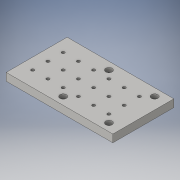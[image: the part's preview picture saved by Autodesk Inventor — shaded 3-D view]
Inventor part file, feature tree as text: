
AUTODESK INVENTOR PART (.ipt)
format: ipt  version: 2016 (Build 200138000, 138)  size: 142,336 bytes
history: native  units: mm
features: sketch x3, hole x2, projected_geometry x2, extrude x1
ambient origin geometry x8: Origin, YZ Plane, XZ Plane, XY Plane, X Axis, Y Axis, Z Axis, Center Point
bodies: Solid1 (feature_tree)
feature tree (8):
  extrude  "Extrusion1"  Depth=100.0mm
  hole  "Hole1"  [1 undecoded]
  hole  "Hole2"  [1 undecoded]
  sketch  "Sketch1"  dims[d0=100.0mm d1=56.5mm]
  sketch  "Sketch2"  dims[d2=175.0mm d3=12.5mm d4=0.0mm]
  projected_geometry  "Projected Loop1"
  sketch  "Sketch3"  dims[d5=75.0mm d6=75.0mm d7=6.0mm d8=6.0mm d9=10.5mm d10=7.0mm d11=90.0deg d12=8.0mm d13=20.594885mm d14=25.0mm d15=25.0mm d16=60.0mm d18=25.0mm d19=30.0mm d21=25.0mm d24=4.917mm d25=12.0mm d26=10.5mm d27=7.0mm d28=90.0deg d29=8.0mm d30=20.594885mm]
  projected_geometry  "Projected Loop2"
note: 2 required parameter values undecoded (feature->parameter linkage not recoverable at this tier; creation-order binding heuristic only, values carry confidence <= 0.55)
